# Revit family: PRD_FrankeWS_WCSqttngPns_CAMPUSSquatPan_CMPX502N_CMPX503N
name_source: partatom
category: Plumbing Fixtures
revit_build: Autodesk Revit 2018 (Build: 20190510_1515(x64)
units: mm (PartAtom-declared; Revit-internal decimal feet)

## family parameters
Cut with Voids When Loaded = Yes
Host = Face
OmniClass Number = 23.45.05.21.11.21
OmniClass Title = Urinals
Part Type = Normal
Room Calculation Point = No
Round Connector Dimension = Use Diameter
Shared = Yes

## types (2) — shared parameters
AssetType = Fixed
Category = Pr_40_20_93_96, WC squatting pans
Default Elevation = 1100 mm
DiameterNominal = 100  [stored 0.328084 ft]
DurationUnit = year
Features = stainless steel, surface satin finished, suitable for recessed mounting into floor
Finish = Satin finished
GeneralMaterial = PRD_AR_StainlessSteel_SatinFinished
GrossWeight = 9.30 kg
IfcExportAs = IfcSanitaryTerminalType
IfcExportType = URINAL
IntakeSize = 40  [stored 0.131234 ft]
Manufacturer = KWC Group AG
ManufacturerName = KWC Group AG
ManufacturerURL = www.kwc.com
Material = Stainless steel
MaterialCode = 1.4301 Chrome Nickel steel V2A
MaterialThickness = 1.20 mm
MinimumFlushingCapacity = 6.00 liter
Mounting = Pedestal
NetWeight = 8.30 kg
NominalDepth = 700 mm  [stored 2.29659 ft]
NominalHeight = 235 mm  [stored 0.770997 ft]
NominalWidth = 700 mm  [stored 2.29659 ft]
OutletSize = DN 100
ProductInformation = https://pim.kwc.com
Size = 700 x 235 x 700 mm (W x H x D)
TypeOfMounting = Inset floor mounting
TypeOfToiletSeat = No seat
TypeOfWC = Squat-pan
URL = www.kwc.com
Uniclass2015Code = Pr_40_20_93_96
Uniclass2015Title = WC squatting pans
Uniclass2015Version = Products v1.17
UrinalType = Slab
Version = 1
WarrantyDurationUnit = year
zero-valued in all types: SpilloverLevel

## per-type parameters (varying)
| type | BIMObjectName | Description | InletSize | ModelNumber | Name | ProductCode | Spreader | n |
| CMPX502N | PRD_AR_WCSquattingPans_CAMPUSSquatPan_CMPX502N | Squat pan for recessed or inset mounting, stainless steel, surface satin finished, material thickness 1.2 mm, DN 100 waste, drainage into ground, slip resistant patterned foot tread plate areas, suitable for recessed mounting into floor. With spreader for connection of 40 mm outer diameter flushing pipe. | DN 40 | 2030018490 | CAMPUS Squat pan CMPX502N | 205.0000.039 | Yes | 3 |
| CMPX503N | PRD_AR_WCSquattingPans_CAMPUSSquatPan_CMPX503N | Squat pan for recessed or inset mounting, stainless steel, surface satin finished, material thickness 1.2 mm, DN 100 waste, drainage into ground, slip resistant patterned foot tread plate areas, suitable for recessed mounting into floor. Without Spreader or Inlet Hole. |  | 2030023692 | CAMPUS Squat pan CMPX503N | 205.0000.040 | No | 2 |

note: column(s) folded — value = type name in every type: Model, ModelReference

note: [stored X ft] marks values corroborated as IEEE doubles in the binary element streams (Revit-internal decimal feet)

## geometry (parser evidence)
native form markers: Sweep x5
no freeform markers — native parametric forms only
